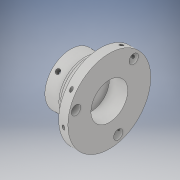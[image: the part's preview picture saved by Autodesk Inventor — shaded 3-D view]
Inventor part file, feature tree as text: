
AUTODESK INVENTOR PART (.ipt)
format: ipt  version: 2019 (Build 230136000, 136)  size: 386,048 bytes
history: native  units: in
note: dims shown in document units (in); Inventor stores cm internally (conversion verified against a paired STEP export)
features: sketch x22, extrude x11, plane x8, mirror x4, projected_geometry x4, pattern_circular x2, thread x2, fillet x2, revolve x1, sweep x1
ambient origin geometry x8: Origin, YZ Plane, XZ Plane, XY Plane, X Axis, Y Axis, Z Axis, Center Point
bodies: Solid1 (feature_tree), Solid2 (feature_tree)
feature tree (57):
  extrude  "Extrusion1"  Depth=0.7874in
  extrude  "Extrusion3"  Depth=1.2402in
  extrude  "Extrusion4"  Depth=1.1811in TaperAngle=0.0deg
  pattern_circular  "Circular Pattern1"  Count=4 Angle=360.0deg
  sketch  "Sketch6"  dims[d16=0.3937in d17=45.0deg]
  plane  "Work Plane1"
  extrude  "Extrusion5"  TaperAngle=45.0deg  [1 undecoded]
  plane  "Work Plane2"
  mirror  "Mirror1"
  extrude  "Extrusion6"  TaperAngle=45.0deg  [1 undecoded]
  extrude  "Extrusion7"  Depth=0.2362in TaperAngle=0.0deg
  sketch  "Sketch11"  dims[d26=0.3937in d27=0.0in d28=0.0118in]
  plane  "Work Plane3"
  extrude  "Extrusion8"  TaperAngle=45.0deg  [1 undecoded]
  thread  "Thread1"  [1 undecoded]
  mirror  "Mirror2"
  extrude  "Extrusion9"  Depth=0.3937in
  revolve  "Revolution1"  [1 undecoded]
  mirror  "Mirror3"
  fillet  "Fillet1"  Radius=0.4724in
  fillet  "Fillet2"  Radius=0.0098in
  extrude  "Extrusion10"  Depth=0.4724in
  extrude  "Extrusion11"  Depth=0.3937in TaperAngle=0.0deg
  sketch  "Sketch18"  dims[d46=1.7717in]
  plane  "Work Plane4"
  sketch  "Sketch19"  dims[d47=90.0deg]
  plane  "Work Plane5"
  sketch  "Sketch22"  dims[d48=90.0deg]
  plane  "Work Plane6"
  sketch  "Sketch23"  dims[d49=0.1575in]
  sweep  "Sweep1"
  plane  "Work Plane7"
  thread  "Thread3"  [1 undecoded]
  sketch  "Sketch25"  dims[d51=0.3937in d52=0.0in]
  sketch  "Sketch26"  dims[d53=1.4764in]
  sketch  "Sketch27"  dims[d54=45.0deg]
  plane  "Work Plane10"
  mirror  "Mirror4"
  pattern_circular  "Circular Pattern2"  [2 undecoded]
  extrude  "Extrusion13"  TaperAngle=45.0deg  [1 undecoded]
  sketch  "Sketch2"  dims[d3=0.7874in d4=1.7323in]
  sketch  "Sketch4"  dims[d5=0.4724in d6=0.0in d9=1.2402in]
  sketch  "Sketch5"  dims[d10=0.2008in d11=1.1811in d12=0.0in d13=1.5748in d14=360.0deg]
  sketch  "Sketch7"  dims[d18=0.1181in d19=45.0deg]
  sketch  "Sketch8"  dims[d20=0.3543in d21=0.2362in d22=0.0in]
  projected_geometry  "Projected Loop1"
  sketch  "Sketch9"  dims[d23=0.8661in d24=45.0deg d25=0.2047in]
  sketch  "Sketch12"  dims[d29=0.4724in d30=0.0in d31=0.2362in d32=0.4724in d33=0.0in d34=0.0098in]
  sketch  "Sketch13"  dims[d35=45.0deg d36=0.4724in]
  sketch  "Sketch14"  dims[d37=0.1969in d38=0.3937in d39=0.0in]
  sketch  "Sketch15"  dims[d40=0.3937in d41=0.0in d42=0.1969in d43=0.0in d44=0.5906in]
  projected_geometry  "Projected Loop2"
  sketch  "Sketch17"  dims[d45=180.0deg]
  projected_geometry  "Projected Loop3"
  sketch  "Sketch24"  dims[d50=0.0157in]
  projected_geometry  "Projected Loop4"
  sketch  "Sketch28"  dims[d55=0.3976in d56=0.3937in d57=0.0in d58=45.0deg d59=0.1969in d60=180.0deg d64=1.1811in d65=360.0deg d69=1.5748in d70=120.0deg d71=0.1181in d72=0.0in d73=0.0in d74=-1.5748in d75=0.3937in d76=0.0in d78=1.5748in d79=30.0deg d82=135.0deg d83=1.5748in d84=0.7874in d85=0.0in]
note: 9 required parameter values undecoded (feature->parameter linkage not recoverable at this tier; creation-order binding heuristic only, values carry confidence <= 0.55)